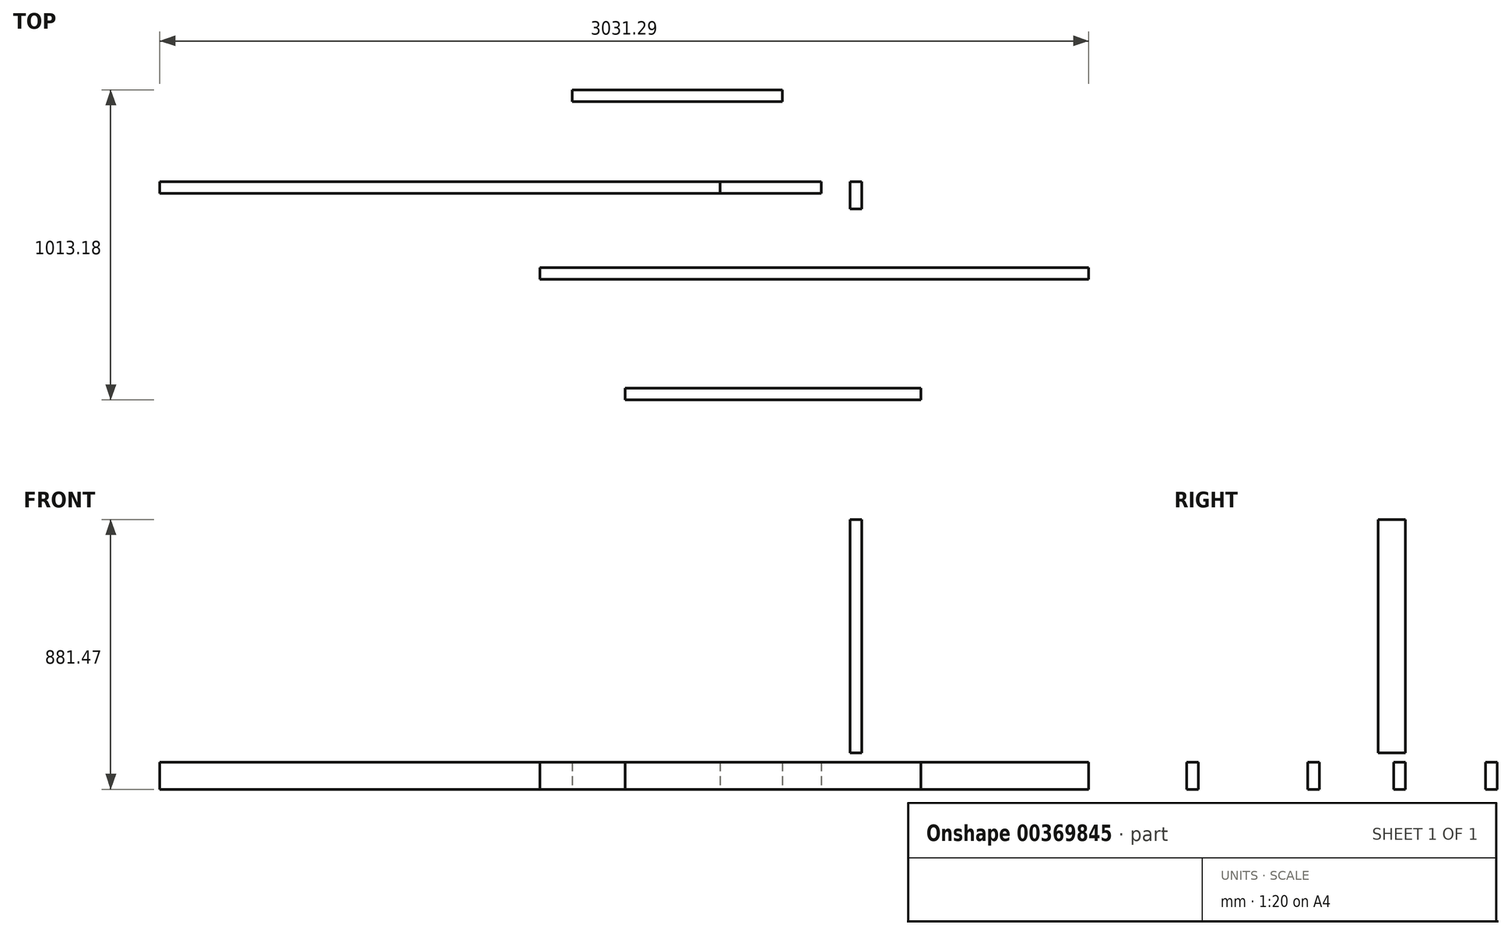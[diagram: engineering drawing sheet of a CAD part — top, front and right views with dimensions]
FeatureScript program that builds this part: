
annotation { "Feature Type Name" : "Feature", "Feature Type Description" : "" }
export const myFeature = defineFeature(function(context is Context, id is Id, definition is map)
    precondition{}
    {
        {
            var Q0;
            Q0=qCreatedBy(makeId("Top.planeOp"),FACE);
            var sketch = newSketch(context, id + "F0", { "sketchPlane" : qUnion([Q0])});
            skLineSegment(sketch, "E0.bottom", {"start": v(0, 0) * mm, "end": v(-1828.8, 0) * mm});
            skLineSegment(sketch, "E0.top", {"start": v(0, -38.1) * mm, "end": v(-1828.8, -38.1) * mm});
            skLineSegment(sketch, "E0.left", {"start": v(0, 0) * mm, "end": v(0, -38.1) * mm});
            skLineSegment(sketch, "E0.right", {"start": v(-1828.8, 0) * mm, "end": v(-1828.8, -38.1) * mm});
            skSolve(sketch);
        }
        {
            var Q0;
            Q0=qSketchRegion(id+"F0",true);
            extrude(context, id + "F1", {"entities" : qUnion([Q0]), "depth" : 88.9 * mm});
        }
        {
            var Q0;
            Q0=qCreatedBy(makeId("Top.planeOp"),FACE);
            var sketch = newSketch(context, id + "F2", { "sketchPlane" : qUnion([Q0])});
            skLineSegment(sketch, "E1.bottom", {"start": v(0, 0) * mm, "end": v(330.2, 0) * mm});
            skLineSegment(sketch, "E1.top", {"start": v(0, -38.1) * mm, "end": v(330.2, -38.1) * mm});
            skLineSegment(sketch, "E1.left", {"start": v(0, 0) * mm, "end": v(0, -38.1) * mm});
            skLineSegment(sketch, "E1.right", {"start": v(330.2, 0) * mm, "end": v(330.2, -38.1) * mm});
            skSolve(sketch);
        }
        {
            var Q0;
            Q0=makeQuery(id+"F2.imprint","IMPRINT",FACE,{"disambiguationData":[TD([[makeQuery(id+"F2.imprint","IMPRINT",EDGE,{"derivedFrom":sQuery(id+"F2.wireOp",EDGE,"E1.bottom")}),-1.0]])]});
            extrude(context, id + "F3", {"entities" : qUnion([Q0]), "depth" : 88.9 * mm});
        }
        {
            var Q0;
            Q0=qCreatedBy(makeId("Top.planeOp"),FACE);
            var sketch = newSketch(context, id + "F4", { "sketchPlane" : qUnion([Q0])});
            skLineSegment(sketch, "E2.bottom", {"start": v(1202.49, -280.94) * mm, "end": v(-588.21, -280.94) * mm});
            skLineSegment(sketch, "E2.top", {"start": v(1202.49, -319.04) * mm, "end": v(-588.21, -319.04) * mm});
            skLineSegment(sketch, "E2.left", {"start": v(1202.49, -280.94) * mm, "end": v(1202.49, -319.04) * mm});
            skLineSegment(sketch, "E2.right", {"start": v(-588.21, -280.94) * mm, "end": v(-588.21, -319.04) * mm});
            skSolve(sketch);
        }
        {
            var Q0;
            Q0=qSketchRegion(id+"F4",true);
            extrude(context, id + "F5", {"entities" : qUnion([Q0]), "depth" : 88.9 * mm});
        }
        {
            var Q0;
            Q0=qCreatedBy(makeId("Top.planeOp"),FACE);
            var sketch = newSketch(context, id + "F6", { "sketchPlane" : qUnion([Q0])});
            skLineSegment(sketch, "E3.bottom", {"start": v(654.4, -675.4) * mm, "end": v(-310.8, -675.4) * mm});
            skLineSegment(sketch, "E3.top", {"start": v(654.4, -713.5) * mm, "end": v(-310.8, -713.5) * mm});
            skLineSegment(sketch, "E3.left", {"start": v(654.4, -675.4) * mm, "end": v(654.4, -713.5) * mm});
            skLineSegment(sketch, "E3.right", {"start": v(-310.8, -675.4) * mm, "end": v(-310.8, -713.5) * mm});
            skSolve(sketch);
        }
        {
            var Q0;
            Q0=qSketchRegion(id+"F6",true);
            extrude(context, id + "F7", {"entities" : qUnion([Q0]), "depth" : 88.9 * mm});
        }
        {
            var Q0;
            Q0=qCreatedBy(makeId("Top.planeOp"),FACE);
            var sketch = newSketch(context, id + "F8", { "sketchPlane" : qUnion([Q0])});
            skLineSegment(sketch, "E4.bottom", {"start": v(-483.42, 299.68) * mm, "end": v(202.38, 299.68) * mm});
            skLineSegment(sketch, "E4.top", {"start": v(-483.42, 261.58) * mm, "end": v(202.38, 261.58) * mm});
            skLineSegment(sketch, "E4.left", {"start": v(-483.42, 299.68) * mm, "end": v(-483.42, 261.58) * mm});
            skLineSegment(sketch, "E4.right", {"start": v(202.38, 299.68) * mm, "end": v(202.38, 261.58) * mm});
            skSolve(sketch);
        }
        {
            var Q0;
            Q0=makeQuery(id+"F8.imprint","IMPRINT",FACE,{"disambiguationData":[TD([[makeQuery(id+"F8.imprint","IMPRINT",EDGE,{"derivedFrom":sQuery(id+"F8.wireOp",EDGE,"E4.bottom")}),-1.0]])]});
            extrude(context, id + "F9", {"entities" : qUnion([Q0]), "depth" : 88.9 * mm});
        }
        {
            var Q0;
            Q0=qCreatedBy(makeId("Front.planeOp"),FACE);
            var sketch = newSketch(context, id + "F10", { "sketchPlane" : qUnion([Q0])});
            skLineSegment(sketch, "E5.bottom", {"start": v(423.23, 881.47) * mm, "end": v(461.33, 881.47) * mm});
            skLineSegment(sketch, "E5.top", {"start": v(423.23, 119.47) * mm, "end": v(461.33, 119.47) * mm});
            skLineSegment(sketch, "E5.left", {"start": v(423.23, 881.47) * mm, "end": v(423.23, 119.47) * mm});
            skLineSegment(sketch, "E5.right", {"start": v(461.33, 881.47) * mm, "end": v(461.33, 119.47) * mm});
            skSolve(sketch);
        }
        {
            var Q0;
            Q0=makeQuery(id+"F10.imprint","IMPRINT",FACE,{"disambiguationData":[TD([[makeQuery(id+"F10.imprint","IMPRINT",EDGE,{"derivedFrom":sQuery(id+"F10.wireOp",EDGE,"E5.bottom")}),-1.0]])]});
            extrude(context, id + "F11", {"entities" : qUnion([Q0]), "depth" : 88.9 * mm});
        }
    });
